# Revit family: Falcon-Table-80TS_1440
name_source: partatom
category: Furniture
revit_build: Autodesk Revit 2017 (Build: 20160225_1515(x64)
units: mm (PartAtom-declared; Revit-internal decimal feet)

## family parameters
Always vertical = Yes
Cut with Voids When Loaded = No
OmniClass Number = 23.40.20.00
OmniClass Title = General Furniture and Specialties
Room Calculation Point = No
Shared = No
Work Plane-Based = No

## types (54) — shared parameters
Assembly Code = E2020200
Description = Descripion
Manufacturer = Manuf
Product Documentation Link = URL
URL = URL

## per-type parameters (varying)
| type | Depth B | Height F | Legs Offset | Model | Width A | with Casters |
| 24 x 48 x 29 | 48.00" | 29.00" | 0.00" | 80ST-1440-244830 | 24.00" | No |
| 24 x 48 x 36 | 48.00" | 36.00" | 0.00" | 80ST-1440-244836 | 24.00" | No |
| 24 x 48 x 42 | 48.00" | 42.00" | 0.00" | 80ST-1440-244842 | 24.00" | No |
| 24 x 60 x 29 | 60.00" | 29.00" | 0.00" | 80ST-1440-246030 | 24.00" | No |
| 24 x 60 x 36 | 60.00" | 36.00" | 0.00" | 80ST-1440-246036 | 24.00" | No |
| 24 x 60 x 42 | 60.00" | 42.00" | 0.00" | 80ST-1440-246042 | 24.00" | No |
| 24 x 72 x 29 | 72.00" | 29.00" | 0.00" | 80ST-1440-247230 | 24.00" | No |
| 24 x 72 x 36 | 72.00" | 36.00" | 0.00" | 80ST-1440-247236 | 24.00" | No |
| 24 x 72 x 42 | 72.00" | 42.00" | 0.00" | 80ST-1440-247242 | 24.00" | No |
| 30 x 48 x 29 | 48.00" | 29.00" | 0.00" | 80ST-1440-304830 | 30.00" | No |
| 30 x 48 x 36 | 48.00" | 36.00" | 0.00" | 80ST-1440-304836 | 30.00" | No |
| 30 x 48 x 42 | 48.00" | 42.00" | 0.00" | 80ST-1440-304842 | 30.00" | No |
| 30 x 60 x 29 | 60.00" | 29.00" | 0.00" | 80ST-1440-306030 | 30.00" | No |
| 30 x 60 x 36 | 60.00" | 36.00" | 0.00" | 80ST-1440-306036 | 30.00" | No |
| 30 x 60 x 42 | 60.00" | 42.00" | 0.00" | 80ST-1440-306042 | 30.00" | No |
| 30 x 72 x 29 | 72.00" | 29.00" | 0.00" | 80ST-1440-307230 | 30.00" | No |
| 30 x 72 x 36 | 72.00" | 36.00" | 0.00" | 80ST-1440-307236 | 30.00" | No |
| 30 x 72 x 42 | 72.00" | 42.00" | 0.00" | 80ST-1440-307242 | 30.00" | No |
| 36 x 48 x 29 | 48.00" | 29.00" | 0.00" | 80ST-1440-364830 | 36.00" | No |
| 36 x 48 x 36 | 48.00" | 36.00" | 0.00" | 80ST-1440-364836 | 36.00" | No |
| 36 x 48 x 42 | 48.00" | 42.00" | 0.00" | 80ST-1440-364842 | 36.00" | No |
| 36 x 60 x 29 | 60.00" | 29.00" | 0.00" | 80ST-1440-366030 | 36.00" | No |
| 36 x 60 x 36 | 60.00" | 36.00" | 0.00" | 80ST-1440-366036 | 36.00" | No |
| 36 x 60 x 42 | 60.00" | 42.00" | 0.00" | 80ST-1440-366042 | 36.00" | No |
| 36 x 72 x 29 | 72.00" | 29.00" | 0.00" | 80ST-1440-367230 | 36.00" | No |
| 36 x 72 x 36 | 72.00" | 36.00" | 0.00" | 80ST-1440-367236 | 36.00" | No |
| 36 x 72 x 42 | 72.00" | 42.00" | 0.00" | 80ST-1440-367242 | 36.00" | No |
| 24 x 48 x 29 wCasters | 48.00" | 29.00" | 5.31" | 80ST-1440-244830-C | 24.00" | Yes |
| 24 x 48 x 36 wCasters | 48.00" | 36.00" | 5.31" | 80ST-1440-244836-C | 24.00" | Yes |
| 24 x 48 x 42 wCasters | 48.00" | 42.00" | 5.31" | 80ST-1440-244842-C | 24.00" | Yes |
| 24 x 60 x 29 wCasters | 60.00" | 29.00" | 5.31" | 80ST-1440-246030-C | 24.00" | Yes |
| 24 x 60 x 36 wCasters | 60.00" | 36.00" | 5.31" | 80ST-1440-246036-C | 24.00" | Yes |
| 24 x 60 x 42 wCasters | 60.00" | 42.00" | 5.31" | 80ST-1440-246042-C | 24.00" | Yes |
| 24 x 72 x 29 wCasters | 72.00" | 29.00" | 5.31" | 80ST-1440-247230-C | 24.00" | Yes |
| 24 x 72 x 36 wCasters | 72.00" | 36.00" | 5.31" | 80ST-1440-247236-C | 24.00" | Yes |
| 24 x 72 x 42 wCasters | 72.00" | 42.00" | 5.31" | 80ST-1440-247242-C | 24.00" | Yes |
| 30 x 48 x 29 wCasters | 48.00" | 29.00" | 5.31" | 80ST-1440-304830-C | 30.00" | Yes |
| 30 x 48 x 36 wCasters | 48.00" | 36.00" | 5.31" | 80ST-1440-304836-C | 30.00" | Yes |
| 30 x 48 x 42 wCasters | 48.00" | 42.00" | 5.31" | 80ST-1440-304842-C | 30.00" | Yes |
| 30 x 60 x 29 wCasters | 60.00" | 29.00" | 5.31" | 80ST-1440-306030-C | 30.00" | Yes |
| 30 x 60 x 36 wCasters | 60.00" | 36.00" | 5.31" | 80ST-1440-306036-C | 30.00" | Yes |
| 30 x 60 x 42 wCasters | 60.00" | 42.00" | 5.31" | 80ST-1440-306042-C | 30.00" | Yes |
| 30 x 72 x 29 wCasters | 72.00" | 29.00" | 5.31" | 80ST-1440-307230-C | 30.00" | Yes |
| 30 x 72 x 36 wCasters | 72.00" | 36.00" | 5.31" | 80ST-1440-307236-C | 30.00" | Yes |
| 30 x 72 x 42 wCasters | 72.00" | 42.00" | 5.31" | 80ST-1440-307242-C | 30.00" | Yes |
| 36 x 48 x 29 wCasters | 48.00" | 29.00" | 5.31" | 80ST-1440-364830-C | 36.00" | Yes |
| 36 x 48 x 36 wCasters | 48.00" | 36.00" | 5.31" | 80ST-1440-364836-C | 36.00" | Yes |
| 36 x 48 x 42 wCasters | 48.00" | 42.00" | 5.31" | 80ST-1440-364842-C | 36.00" | Yes |
| 36 x 60 x 29 wCasters | 60.00" | 29.00" | 5.31" | 80ST-1440-366030-C | 36.00" | Yes |
| 36 x 60 x 36 wCasters | 60.00" | 36.00" | 5.31" | 80ST-1440-366036-C | 36.00" | Yes |
| 36 x 60 x 42 wCasters | 60.00" | 42.00" | 5.31" | 80ST-1440-366042-C | 36.00" | Yes |
| 36 x 72 x 29 wCasters | 72.00" | 29.00" | 5.31" | 80ST-1440-367230-C | 36.00" | Yes |
| 36 x 72 x 36 wCasters | 72.00" | 36.00" | 5.31" | 80ST-1440-367236-C | 36.00" | Yes |
| 36 x 72 x 42 wCasters | 72.00" | 42.00" | 5.31" | 80ST-1440-367242-C | 36.00" | Yes |

## geometry (parser evidence)
native form markers: Sweep x12
no freeform markers — native parametric forms only
